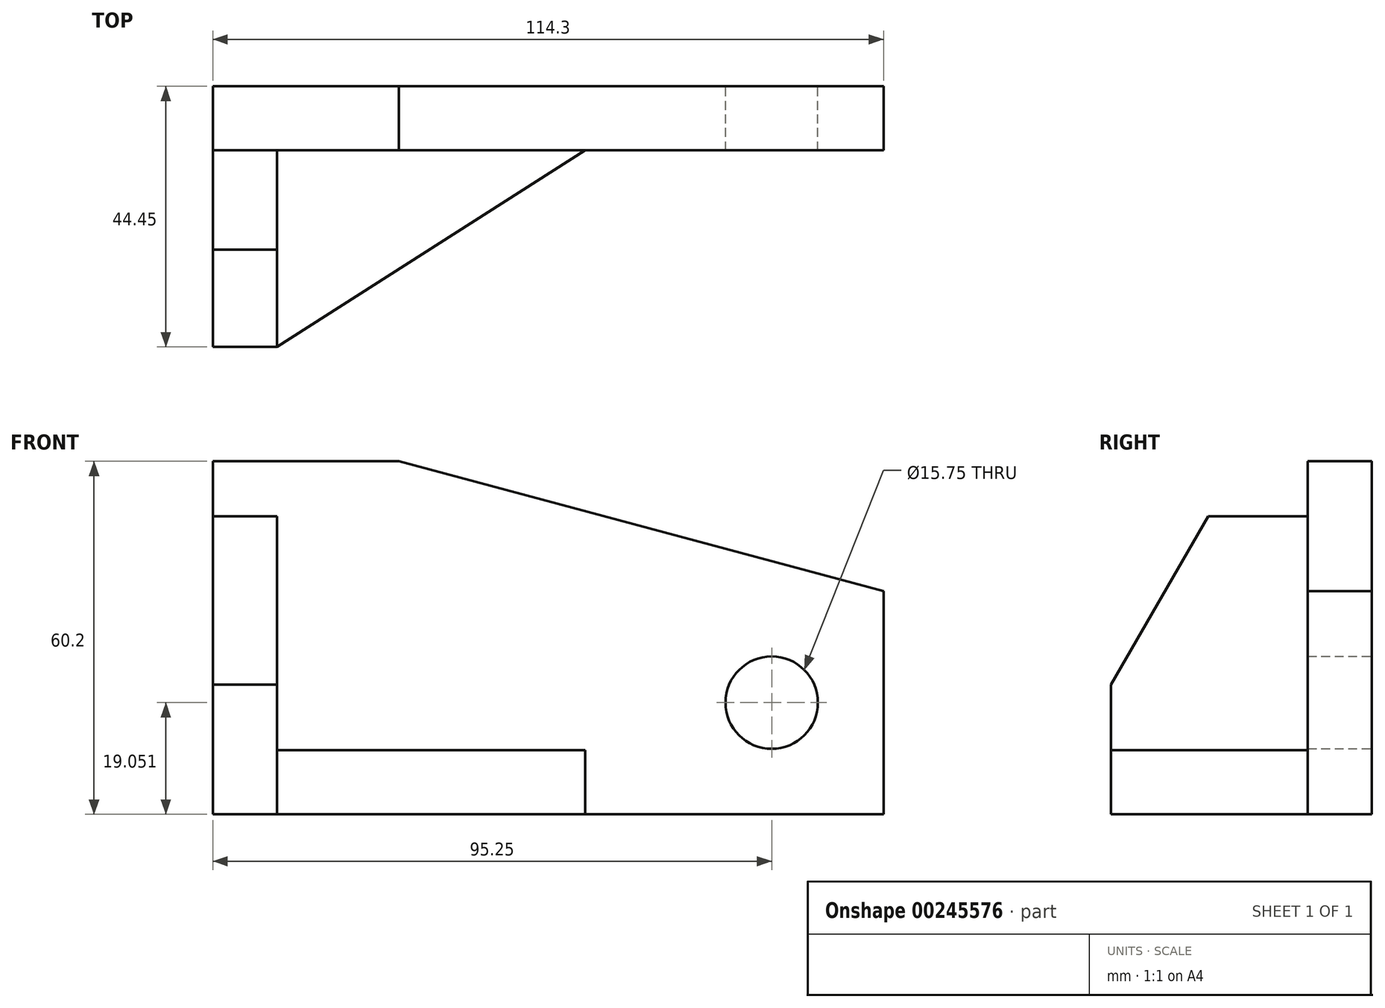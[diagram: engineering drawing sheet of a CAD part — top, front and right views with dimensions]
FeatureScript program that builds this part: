
annotation { "Feature Type Name" : "Feature", "Feature Type Description" : "" }
export const myFeature = defineFeature(function(context is Context, id is Id, definition is map)
    precondition{}
    {
        {
            var Q0;
            Q0=qCreatedBy(makeId("Front.planeOp"),FACE);
            var sketch = newSketch(context, id + "F0", { "sketchPlane" : qUnion([Q0])});
            skLineSegment(sketch, "E0.bottom", {"start": v(-25.4, 30.1) * mm, "end": v(-57.15, 30.1) * mm});
            skLineSegment(sketch, "E0.top", {"start": v(57.15, -30.1) * mm, "end": v(-57.15, -30.1) * mm});
            skLineSegment(sketch, "E0.left", {"start": v(57.15, 7.98) * mm, "end": v(57.15, -30.1) * mm});
            skLineSegment(sketch, "E0.right", {"start": v(-57.15, 30.1) * mm, "end": v(-57.15, -30.1) * mm});
            skPoint(sketch, "E0.middle", {"position": v(0, 0) * mm});
            skLineSegment(sketch, "E1", {"start": v(-57.15, 30.1) * mm, "end": v(-25.4, 30.1) * mm, "construction": true});
            skLineSegment(sketch, "E2", {"start": v(-25.4, 30.1) * mm, "end": v(57.15, 7.98) * mm});
            skLineSegment(sketch, "E3", {"start": v(57.15, -30.1) * mm, "end": v(38.1, -30.1) * mm, "construction": true});
            skLineSegment(sketch, "E4", {"start": v(38.1, -30.1) * mm, "end": v(38.1, -11.05) * mm, "construction": true});
            skCircle(sketch, "E5", {"center": v(38.1, -11.05) * mm, "radius": 7.87 * mm});
            skSolve(sketch);
        }
        {
            var Q0;
            Q0=makeQuery(id+"F0.imprint","IMPRINT",FACE,{"disambiguationData":[TD([[makeQuery(id+"F0.imprint","IMPRINT",EDGE,{"derivedFrom":sQuery(id+"F0.wireOp",EDGE,"E0.bottom")}),1.0]])]});
            extrude(context, id + "F1", {"entities" : qUnion([Q0]), "depth" : 10.92 * mm});
        }
        {
            var Q0;
            Q0=makeQuery(id+"F1.opExtrude","SWEPT_FACE",FACE,{"disambiguationData":[OSD([sQuery(id+"F0.wireOp",EDGE,"E0.right")])]});
            var sketch = newSketch(context, id + "F2", { "sketchPlane" : qUnion([Q0])});
            skLineSegment(sketch, "E6.bottom", {"start": v(10.92, -30.1) * mm, "end": v(44.45, -30.1) * mm});
            skLineSegment(sketch, "E6.top", {"start": v(10.92, 20.7) * mm, "end": v(27.88, 20.7) * mm});
            skLineSegment(sketch, "E6.left", {"start": v(10.92, -30.1) * mm, "end": v(10.92, 20.7) * mm});
            skLineSegment(sketch, "E6.right", {"start": v(44.45, -30.1) * mm, "end": v(44.45, -8) * mm});
            skLineSegment(sketch, "E7", {"start": v(44.45, -30.1) * mm, "end": v(44.45, -8) * mm, "construction": true});
            skLineSegment(sketch, "E8", {"start": v(44.45, -8) * mm, "end": v(27.88, 20.7) * mm});
            skSolve(sketch);
        }
        {
            var Q0;
            Q0=makeQuery(id+"F2.imprint","IMPRINT",FACE,{"disambiguationData":[TD([[makeQuery(id+"F2.imprint","IMPRINT",EDGE,{"derivedFrom":sQuery(id+"F2.wireOp",EDGE,"E6.bottom")}),1.0]])]});
            extrude(context, id + "F3", {"entities" : qUnion([Q0]), "operationType" : NewBodyOperationType.ADD, "oppositeDirection" : true, "depth" : 10.92 * mm});
        }
        {
            var Q0;
            Q0=makeQuery(id+"F3.boolean.opBoolean","MERGE",FACE,{"derivedFrom":[makeQuery(id+"F1.opExtrude","SWEPT_FACE",FACE,{"disambiguationData":[OSD([sQuery(id+"F0.wireOp",EDGE,"E0.top")])]}),makeQuery(id+"F3.opExtrude","SWEPT_FACE",FACE,{"disambiguationData":[OSD([sQuery(id+"F2.wireOp",EDGE,"E6.bottom")])]})]});
            var sketch = newSketch(context, id + "F4", { "sketchPlane" : qUnion([Q0])});
            skLineSegment(sketch, "E9", {"start": v(-57.15, 10.92) * mm, "end": v(6.35, 10.92) * mm, "construction": true});
            skLineSegment(sketch, "E10", {"start": v(-46.23, 44.45) * mm, "end": v(6.35, 10.92) * mm});
            skSolve(sketch);
        }
        {
            var Q0;
            {var subQ0=sQuery(id+"F4.wireOp",EDGE,"E10");Q0=makeQuery(id+"F4.imprint","IMPRINT",FACE,{"disambiguationData":[TD([[makeQuery(id+"F4.imprint","IMPRINT",EDGE,{"derivedFrom":subQ0}),-1.0]])]});}
            extrude(context, id + "F5", {"entities" : qUnion([Q0]), "operationType" : NewBodyOperationType.ADD, "oppositeDirection" : true, "depth" : 10.92 * mm});
        }
    });
